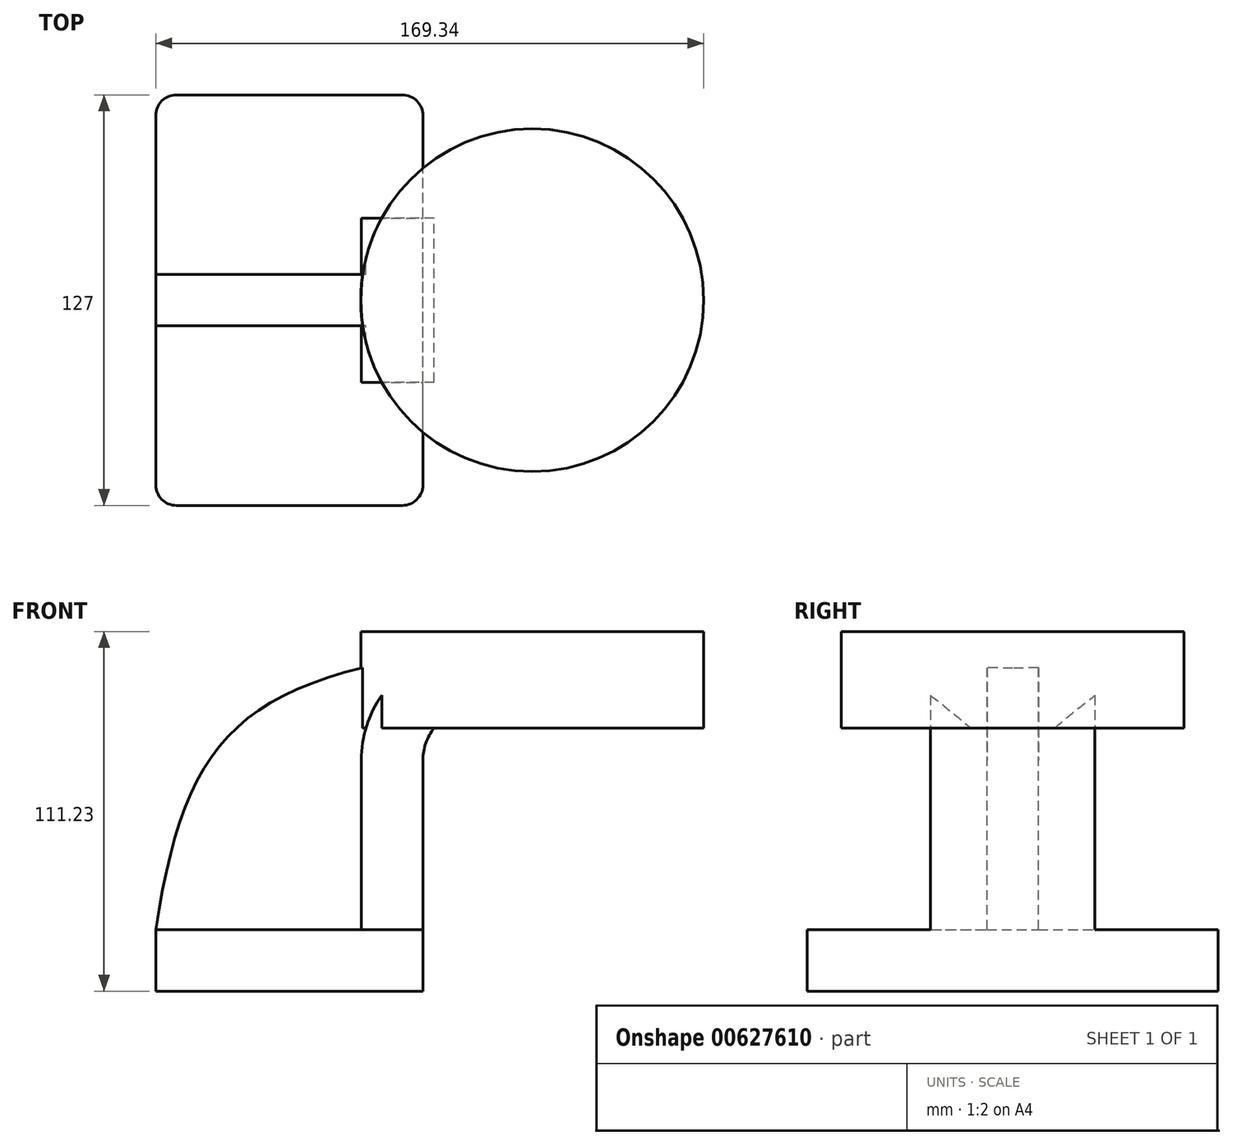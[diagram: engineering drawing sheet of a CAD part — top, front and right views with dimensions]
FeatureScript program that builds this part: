
annotation { "Feature Type Name" : "Feature", "Feature Type Description" : "" }
export const myFeature = defineFeature(function(context is Context, id is Id, definition is map)
    precondition{}
    {
        {
            var Q0;
            Q0=qCreatedBy(makeId("Front.planeOp"),FACE);
            var sketch = newSketch(context, id + "F0", { "sketchPlane" : qUnion([Q0])});
            skLineSegment(sketch, "E0.bottom", {"start": v(-41.28, 9.52) * mm, "end": v(41.28, 9.53) * mm});
            skLineSegment(sketch, "E0.top", {"start": v(-41.28, -9.53) * mm, "end": v(41.28, -9.53) * mm});
            skLineSegment(sketch, "E0.left", {"start": v(-41.28, 9.52) * mm, "end": v(-41.27, -9.53) * mm});
            skLineSegment(sketch, "E0.right", {"start": v(41.28, 9.53) * mm, "end": v(41.28, -9.52) * mm});
            skPoint(sketch, "E0.middle", {"position": v(0, 0) * mm});
            skLineSegment(sketch, "E1", {"start": v(41.27, 9.53) * mm, "end": v(41.27, 61.93) * mm});
            skArc(sketch, "E2", {"start": v(41.27, 61.93) * mm, "mid": v(45.92, 73.15) * mm, "end": v(57.15, 77.8) * mm});
            skLineSegment(sketch, "E3", {"start": v(57.15, 77.8) * mm, "end": v(74.92, 77.8) * mm});
            skLineSegment(sketch, "E4.0", {"start": v(57.15, 96.85) * mm, "end": v(74.92, 96.85) * mm});
            skArc(sketch, "E4.1", {"start": v(22.22, 61.93) * mm, "mid": v(32.45, 86.62) * mm, "end": v(57.15, 96.85) * mm});
            skLineSegment(sketch, "E4.2", {"start": v(22.22, 9.53) * mm, "end": v(22.22, 61.93) * mm});
            skLineSegment(sketch, "E5", {"start": v(74.92, 77.8) * mm, "end": v(74.92, 96.85) * mm});
            skFitSpline(sketch, "E6", {"points": [v(-41.28, 9.52) * mm, v(57.15, 96.85) * mm], "startDerivative": vector(28, 182.49) * mm, "endDerivative": vector(218.11, 29.46) * mm});
            skLineSegment(sketch, "E7.bottom", {"start": v(128.06, 71.88) * mm, "end": v(75.06, 71.88) * mm});
            skLineSegment(sketch, "E7.top", {"start": v(128.06, 101.7) * mm, "end": v(75.06, 101.7) * mm});
            skLineSegment(sketch, "E7.left", {"start": v(128.06, 71.88) * mm, "end": v(128.06, 101.7) * mm});
            skPoint(sketch, "E7.middle", {"position": v(101.56, 86.79) * mm});
            skLineSegment(sketch, "E8", {"start": v(75.06, 71.88) * mm, "end": v(75.06, 101.7) * mm});
            skSolve(sketch);
        }
        {
            var Q0;
            Q0=makeQuery(id+"F0.imprint","IMPRINT",FACE,{"disambiguationData":[TD([[makeQuery(id+"F0.imprint","IMPRINT",EDGE,{"derivedFrom":sQuery(id+"F0.wireOp",EDGE,"E0.top")}),1.0]])]});
            extrude(context, id + "F1", {"entities" : qUnion([Q0]), "endBound" : BoundingType.SYMMETRIC, "depth" : 127 * mm, "offsetDistance" : 25.4 * mm});
        }
        {
            var Q0;
            {var subQ0=sQuery(id+"F0.wireOp",EDGE,"E1");Q0=makeQuery(id+"F0.imprint","IMPRINT",FACE,{"disambiguationData":[TD([[makeQuery(id+"F0.imprint","IMPRINT",EDGE,{"derivedFrom":subQ0}),1.0]])]});}
            extrude(context, id + "F2", {"entities" : qUnion([Q0]), "operationType" : NewBodyOperationType.ADD, "endBound" : BoundingType.SYMMETRIC, "depth" : 50.8 * mm, "offsetDistance" : 25.4 * mm});
        }
        {
            var Q0;
            {var subQ3=sQuery(id+"F0.wireOp",EDGE,"E4.2");Q0=makeQuery(id+"F0.imprint","IMPRINT",FACE,{"disambiguationData":[TD([[makeQuery(id+"F0.imprint","IMPRINT",EDGE,{"derivedFrom":subQ3}),1.0]])]});}
            extrude(context, id + "F3", {"entities" : qUnion([Q0]), "operationType" : NewBodyOperationType.ADD, "endBound" : BoundingType.SYMMETRIC, "depth" : 15.88 * mm, "offsetDistance" : 25.4 * mm});
        }
        {
            var Q0;
            Q0=makeQuery(id+"F0.imprint","IMPRINT",FACE,{"disambiguationData":[TD([[makeQuery(id+"F0.imprint","IMPRINT",EDGE,{"derivedFrom":sQuery(id+"F0.wireOp",EDGE,"E7.bottom")}),-1.0]])]});
            var Q1;
            Q1=sQuery(id+"F0.wireOp",EDGE,"E8");
            var Q2;
            Q2=sQuery(id+"F0.wireOp",EDGE,"E8");
            revolve(context, id + "F4", {"operationType" : NewBodyOperationType.ADD, "entities" : qUnion([Q0]), "surfaceEntities" : qUnion([Q1]), "axis" : qUnion([Q2]), "revolveType" : RevolveType.FULL});
        }
        {
            var Q0;
            Q0=makeQuery(id+"F1.opExtrude","CAP_EDGE",EDGE,{"disambiguationData":[OSD([sQuery(id+"F0.wireOp",EDGE,"E0.right")])],"isStart":false});
            var Q1;
            Q1=makeQuery(id+"F1.opExtrude","CAP_EDGE",EDGE,{"disambiguationData":[OSD([sQuery(id+"F0.wireOp",EDGE,"E0.left")])],"isStart":false});
            var Q2;
            Q2=makeQuery(id+"F1.opExtrude","CAP_EDGE",EDGE,{"disambiguationData":[OSD([sQuery(id+"F0.wireOp",EDGE,"E0.right")])],"isStart":true});
            var Q3;
            Q3=makeQuery(id+"F1.opExtrude","CAP_EDGE",EDGE,{"disambiguationData":[OSD([sQuery(id+"F0.wireOp",EDGE,"E0.left")])],"isStart":true});
            fillet(context, id + "F5", {"entities" : qUnion([Q0, Q1, Q2, Q3]), "radius" : 6.35 * mm, "tangentPropagation" : true, "allowEdgeOverflow" : false});
        }
    });
